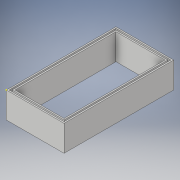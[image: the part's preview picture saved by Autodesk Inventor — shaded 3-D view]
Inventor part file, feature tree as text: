
AUTODESK INVENTOR PART (.ipt)
format: ipt  version: 2017 (Build 210142000, 142)  size: 201,728 bytes
history: native  units: in
note: dims shown in document units (in); Inventor stores cm internally (conversion verified against a paired STEP export)
features: extrude x5, sketch x5, plane x2, mirror x2, other x1
ambient origin geometry x8: Origin, YZ Plane, XZ Plane, XY Plane, X Axis, Y Axis, Z Axis, Center Point
bodies: Solid1 (feature_tree)
feature tree (15):
  extrude  "Extrusion1"  Depth=76.0in
  extrude  "Extrusion3"  Depth=1.0in
  extrude  "Extrusion4"  Depth=1.0in
  plane  "Work Plane1"
  mirror  "Mirror1"
  plane  "Work Plane2"
  extrude  "Extrusion5"  Depth=2.0in TaperAngle=0.0deg
  mirror  "Mirror2"
  sketch  "Sketch11"  dims[d16=1.0in d17=2.0in d18=0.0in]
  extrude  "Extrusion6"  Depth=18.0in
  sketch  "Sketch1"  dims[d0=40.0in d1=76.0in]
  sketch  "Sketch8"  dims[d2=18.0in d3=0.0in d13=1.0in]
  other  "InnerInset1"
  sketch  "Sketch10"  dims[d14=1.0in d15=1.0in]
  sketch  "Sketch12"  dims[d19=10.0in d20=18.0in d21=18.0in d22=10.0in d23=2.0in d24=0.0in d25=7.0in d26=7.0in d27=6.0in d28=2.0in d29=0.0in d30=1.0in d31=1.0in d32=24.0in d33=0.0in]
